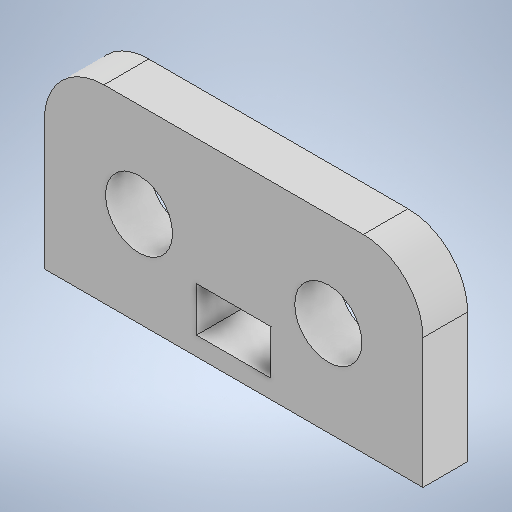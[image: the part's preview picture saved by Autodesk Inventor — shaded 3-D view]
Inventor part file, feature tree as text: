
AUTODESK INVENTOR PART (.ipt)
format: ipt  version: 2025.1 (Build 291241020, 241B)  size: 234,496 bytes
history: native  units: mm
features: extrude x2, sketch x2, fillet x1, hole x1
ambient origin geometry x8: Origin, YZ Plane, XZ Plane, XY Plane, X Axis, Y Axis, Z Axis, Center Point
bodies: Solid1 (feature_tree)
feature tree (6):
  extrude  "Extrusion1"  Depth=12.7mm
  fillet  "Fillet1"  Radius=3.0mm
  sketch  "Sketch2"  dims[d4=4.0mm d10=5.0mm d11=3.0mm d12=1.25mm d13=0.0mm d14=0.0mm d15=6.35mm d16=6.35mm d17=6.35mm d18=4.5mm d19=6.0mm d20=9.4mm d21=2.0mm d22=90.0deg d23=8.0mm d24=20.594885mm]
  extrude  "Extrusion2"  Depth=5.0mm
  hole  "Hole1"  [1 undecoded]
  sketch  "Sketch1"  dims[d0=25.4mm d1=12.7mm d2=3.0mm d3=0.0mm]
note: 1 required parameter value undecoded (feature->parameter linkage not recoverable at this tier; creation-order binding heuristic only, values carry confidence <= 0.55)
